# Revit family: LB Lounge 3 seaters
name_source: partatom
category: Furniture
units: mm (PartAtom-declared; Revit-internal decimal feet)

## family parameters
Always vertical = Yes
Cut with Voids When Loaded = No
OmniClass Number = 23.40.20.00
OmniClass Title = General Furniture and Specialties
Room Calculation Point = No
Shared = No
Work Plane-Based = No

## types (12) — shared parameters
Default Elevation = 0' - 0"
Manufacturer = AIS Inc
Product = LB LOUNGE 3 SEATERS
URL = https://www.ais-inc.com

## per-type parameters (varying)
| type | Description |
| F-SSC346630C | 66Wx30Dx34H Configurable LB Lounge Open Base 3-Seater (6-Cushion) |
| F-SSC347230C | 72Wx30Dx34H Configurable LB Lounge Open Base 3-Seater (6-Cushion) |
| F-SSC426630C | 66Wx30Dx42H Configurable LB Lounge Open Base 3-Seater (6-Cushion) |
| F-SSC427230C | 72Wx30Dx42H Configurable LB Lounge Open Base 3-Seater (6-Cushion) |
| F-SSC506630C | 66Wx30Dx50H Configurable LB Lounge Open Base 3-Seater (6-Cushion) |
| F-SSC507230C | 72Wx30Dx50H Configurable LB Lounge Open Base 3-Seater (6-Cushion) |
| F-SSS346630C | 66Wx30Dx34H Configurable LB Lounge Solid Base 3-Seater (6-Cushion) |
| F-SSS347230C | 72Wx30Dx34H  Configurable LB Lounge Solid Base 3-Seater (6-Cushion) |
| F-SSS426630C | 66Wx30Dx42H Configurable LB Lounge Solid Base 3-Seater (6-Cushion) |
| F-SSS427230C | 72Wx30Dx42H Configurable LB Lounge Solid Base 3-Seater (6-Cushion) |
| F-SSS506630C | 66Wx30Dx50H Configurable LB Lounge Solid Base 3-Seater (6-Cushion) |
| F-SSS507230C | 72Wx30Dx50H Configurable LB Lounge Solid Base 3-Seater (6-Cushion) |

note: column(s) folded — value = type name in every type: Model

type visibility flags: 12 boolean params named "<type name>" — each type sets only its own to Yes (folded from table)

## geometry (parser evidence)
native form markers: Sweep x3
no freeform markers — native parametric forms only
